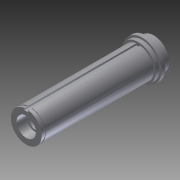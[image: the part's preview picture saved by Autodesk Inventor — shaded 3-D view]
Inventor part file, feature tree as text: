
AUTODESK INVENTOR PART (.ipt)
format: ipt  version: 2012 (Build 160160000, 160)  size: 155,648 bytes
history: native  units: in
note: dims shown in document units (in); Inventor stores cm internally (conversion verified against a paired STEP export)
features: extrude x8, sketch x6, plane x5
ambient origin geometry x8: Origin, YZ Plane, XZ Plane, XY Plane, X Axis, Y Axis, Z Axis, Center Point
feature tree (19):
  sketch  "Sketch1"  dims[d0=1.0in d4=0.5in]
  extrude  "Extrusion4"  Depth=0.5in
  plane  "Work Plane5"
  extrude  "Extrusion8"  [1 undecoded]
  plane  "Work Plane6"
  plane  "Work Plane9"
  plane  "Work Plane10"
  extrude  "Extrusion16"  Depth=0.045in TaperAngle=0.0deg
  extrude  "Extrusion17"  Depth=0.546in
  extrude  "Extrusion18"  Depth=0.125in
  plane  "Work Plane13"
  sketch  "Sketch16"  dims[d50=0.125in d51=0.125in]
  extrude  "Extrusion19"  Depth=0.5625in
  extrude  "Extrusion20"  Depth=0.045in TaperAngle=0.0deg
  extrude  "Extrusion21"  Depth=0.625in
  sketch  "Sketch6"  dims[d9=4.125in d10=0.0in d23=-0.125in]
  sketch  "Sketch14"  dims[d24=0.96in d25=0.045in d26=0.0in]
  sketch  "Sketch15"  dims[d27=-0.595in d36=-1.706in d39=0.546in]
  sketch  "Sketch17"  dims[d52=0.0625in d53=0.5625in d54=0.045in d55=0.0in d56=0.625in d57=0.3125in d58=0.0in d59=0.625in d60=0.3125in d61=0.0in d62=-0.25in d63=1.25in d64=0.125in d65=0.0in d66=0.25in d67=0.0in d68=1.125in d69=0.25in d70=0.0in]
note: 1 required parameter value undecoded (feature->parameter linkage not recoverable at this tier; creation-order binding heuristic only, values carry confidence <= 0.55)
